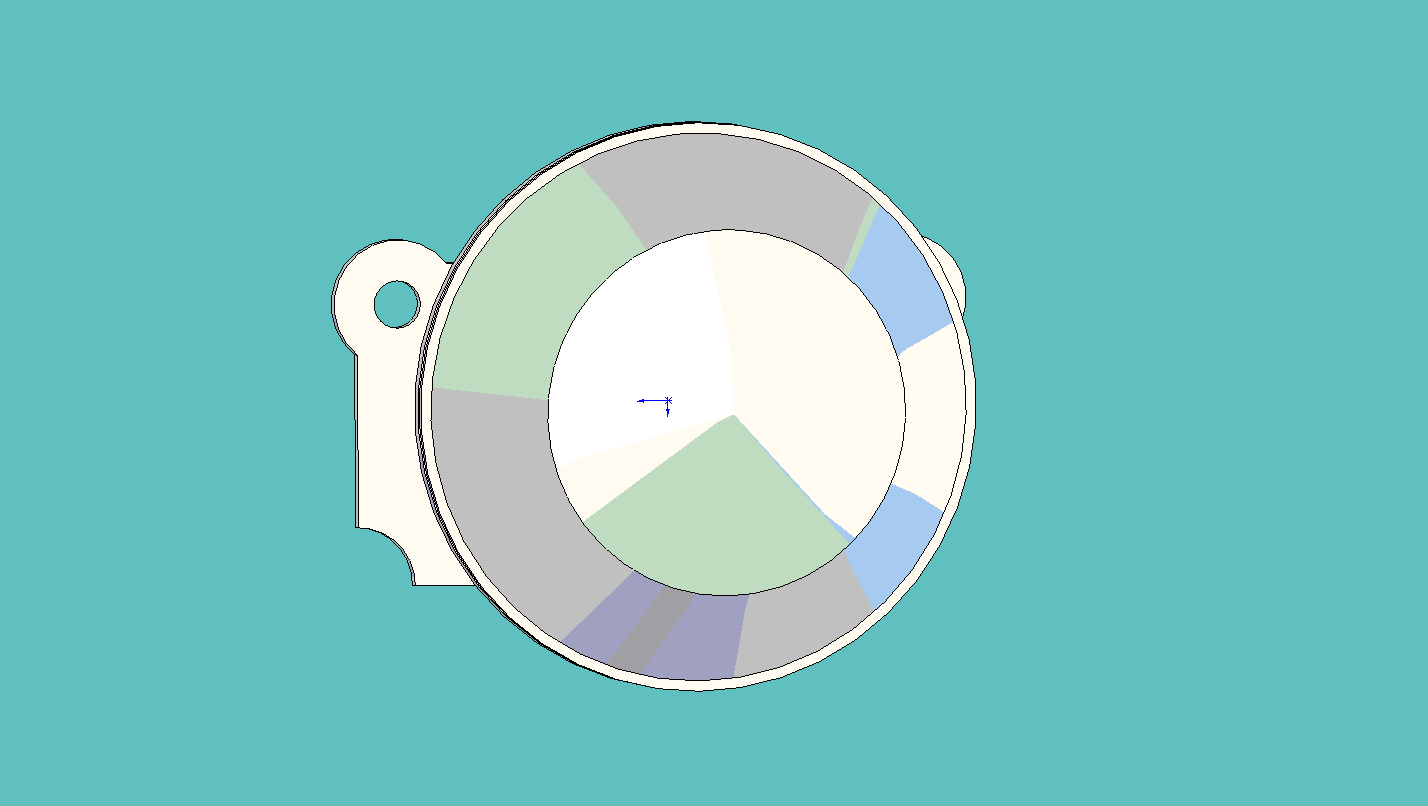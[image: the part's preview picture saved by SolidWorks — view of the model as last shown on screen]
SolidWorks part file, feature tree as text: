
SOLIDWORKS PART (.sldprt)
format: sldprt  version: not decoded by parser v0  size: 289,280 bytes
history: native  units: mm
features: sketch x6, cut_extrude x3, extrude x2, fillet x2, material x1, revolve x1, plane x1 (+13 scaffold rows collapsed)
feature tree (29):
  scaffold x13  (default folders/planes/origin — collapsed)
  material  "Material <not specified>"
  sketch  "Sketch1"  dims[D1=~57.451229mm]
  revolve  "Revolve1"  Angle=360deg
  sketch  "Sketch2"  dims[D1=5.08mm]
  extrude  "Extrude1"  Depth=15.24mm
  fillet  "Fillet1"  Radius=2.54mm
  plane  "Plane1"  Offset=0mm
  sketch  "Sketch3"  dims[D1=7.62mm]
  extrude  "Extrude2"  Depth=2.54mm
  sketch  "Sketch4"  dims[D1=8.89mm]
  cut_extrude  "Cut-Extrude1"  [1 undecoded]
  fillet  "Fillet2"  Radius=2.54mm
  sketch  "Sketch5"
  cut_extrude  "Cut-Extrude2"  Depth=2.54mm
  sketch  "Sketch6"  dims[D1=5.08mm]
  cut_extrude  "Cut-Extrude3"  Depth=30.48mm
decode coverage: 12 of 14 modeling features carry decoded parameters
note: ~ marks probable driven/reference dimensions
note: 1 parameter value undecoded
note: suppression state not decoded; provenance and decode notes live in map.json
